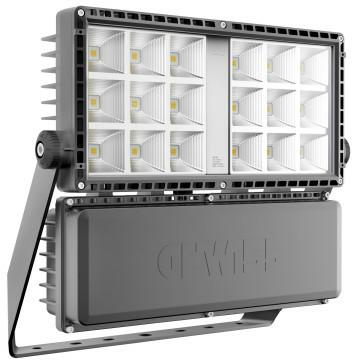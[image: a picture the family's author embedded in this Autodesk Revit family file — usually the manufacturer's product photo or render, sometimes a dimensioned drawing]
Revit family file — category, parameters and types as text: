
# Revit family: Lighting-Proiezione-GEWISS-SMART[PRO]2.0-PROIETTORI-LED-MEDIA-POTENZA_2MODULI_DALI_CLII
name_source: partatom
category: Apparecchi per illuminazione
units: mm (PartAtom-declared; Revit-internal decimal feet)

## family parameters
Condiviso = No
Host = Superficie
Punto di calcolo locali = No
Quota connettore circolare = Usa diametro
Sorgente d'illuminazione = No
Taglio con vuoti quando caricato = No
Tipo di parte = Normale

## types (1)
- Lighting-Proiezione-GEWISS-SMART[PRO]2.0-PROIETTORI-LED-MEDIA-POTENZA_2MODULI_DALI_CLII
    Alimentatore = Incluso
    Apparecchio a ridotta temperatura superficiale = No
    Applicazione = Interno / Esterno
    Cablaggio = Connettore stagno
    Caratteristiche elettriche e gestione della luce = -
    Caratteristiche ottiche e illuminotecniche = -
    Catalogo = LIGHTING
    Certificazione DIN 18032-3 = Si
    Certificazioni e classificazioni = -
    Classe fotobiologica = -
    Classe isolamento = II
    Classificazione: = -
    Codice digitale univoco (Datamatrix) = Attualmente non presente
    Colore = Grigio grafite
    Contesto = Illuminazione di grandi aree, impianti sportivi
    Controllo abbagliamento e luminanza = G*6 - ULOR = 0
    Corpo = Alluminio pressofuso
    Descrizione = SMARTPRO2.0 2M 4000K CRI80 A3 DALI CL2
    Dispositivo di protezione = DM 6 kV / CM 10 kV
    Durata di vita = L90B10 (Tq+25°C) - 40000h L90B10 (Tq+50°C) = 32000h L80B10 (Tq+25°C) - 90000h
    Efficienza luminosa (lm/W) = 113
    Finitura colore = Verniciato a polvere poliestere
    Fissaggio = Staffa
    Frequenza nominale (Hz) = 50 / 60
    GW - Codice Electrocod = 2424
    Gancio di chiusura = Viti metriche esagonali
    Garanzia = 5 anni
    Grado di protezione = IP66
    Gruppo ottico = Parabola in alluminio anodizzato brillantato con alluminio puro 99,99%
    Guarnizioni = silicone antinvecchiamento
    IDF = ff2f1168-8e46-4ea7-9efd-30bc27e4a1fa
    IDT = 132314cb1b854b53a35eaeb109d835d9
    IPEA = STRADALE = A // GRANDI AREE = A3+ // CICLOPEDONALI = A+ // AREE VERDI = A+ // CENTRO STORICO = A5+ // ALTRO = A5+
    Immagine tipo = GWP2274AD.jpg
    Inclinazione = Rotazione su staffa con goniometro integrato
    Indice di resa cromatica = CRI-80
    Informazioni generali = -
    Installazione e manutenzione = -
    Lampada = LED
    Lumen output (lm) = 37200
    Materiali = -
    Modello = GWP2284NB
    Norma di riferimento = EN60598-1; EN60598-2-5; IEC 62778; IEC 62471; EN13201
    Ottica = A3 - Asimmetrica Stretta
    Peso (kg): = 13
    Potenza di sistema = 330W
    Produttore = GEWISS S.p.A.
    Prospetto di default = 1219 mm
    Resistenza agli urti = IK08
    Resistenza al filo incandescente = -
    SEO = Proiettore
    Scheda Tecnica = https://www.gewiss.com
    Schermo = Vetro piano extrachiaro spessore 4mm
    Sistema di controllo = DALI
    Sostituibilità gruppo ottico = Non disponibile
    Sostituibilità piastra di cablaggio = Non disponibile
    Spostamento_x = 2186 mm
    Spostamento_x_effettivo = 1814 mm
    Superficie massima esposta al vento : = 0,170 m2
    Temperatura di colore = 4000K
    Temperatura di esercizio = -30 +50 °C
    Temperatura di stoccaggio = -
    Tensione di alimentazione = 220 - 240 V
    Tipo di apparecchio = Apparecchio per proiezione LED di piccola, media e alta potenza
    Tipo di installazione e montaggio = Torrefaro - Parete - Terra
    Tipologia sorgente luminosa = LED - Non sostituibile
    Tolleranza cromatica = SDCM = 3
    URL = https://www.gewiss.com
    Vano di alimentazione = Integrato
    Versione file RFA = 20.11
    Versioni = Luce naturale 4000K
    Viti esterne = Acciaio inossidabile
